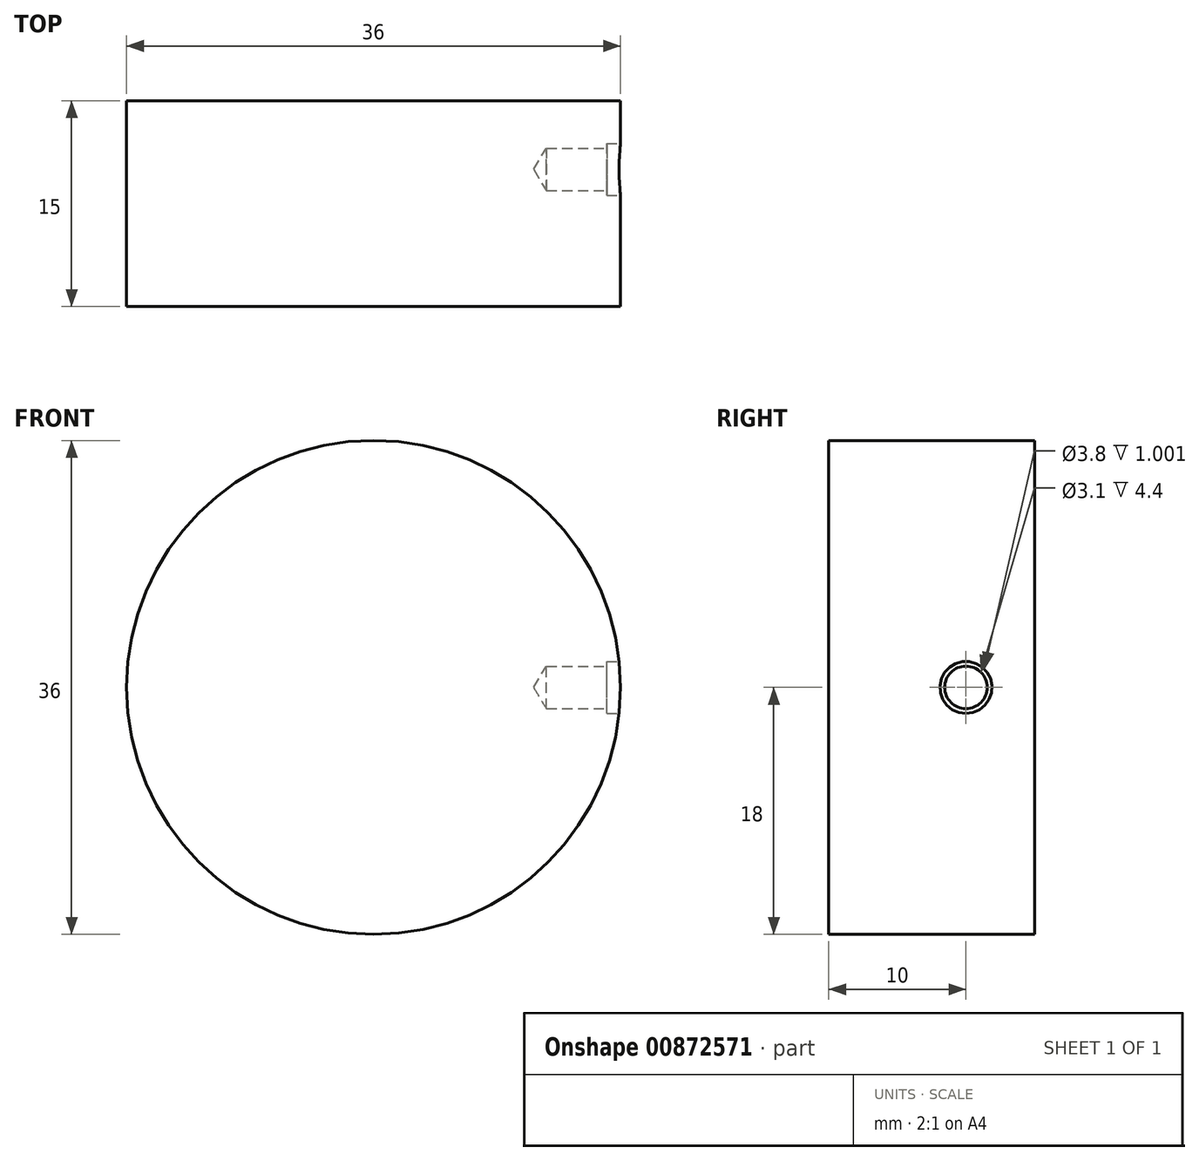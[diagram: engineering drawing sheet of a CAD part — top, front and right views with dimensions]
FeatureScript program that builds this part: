
annotation { "Feature Type Name" : "Feature", "Feature Type Description" : "" }
export const myFeature = defineFeature(function(context is Context, id is Id, definition is map)
    precondition{}
    {
        {
            var Q0;
            Q0=qCreatedBy(makeId("Front.planeOp"),FACE);
            var sketch = newSketch(context, id + "F0", { "sketchPlane" : qUnion([Q0])});
            skCircle(sketch, "E0", {"center": v(0, 0) * mm, "radius": 18 * mm});
            skSolve(sketch);
        }
        {
            var Q0;
            Q0=makeQuery(id+"F0.imprint","IMPRINT",FACE,{"disambiguationData":[TD([[makeQuery(id+"F0.imprint","IMPRINT",EDGE,{"derivedFrom":sQuery(id+"F0.wireOp",EDGE,"E0")}),1.0]])]});
            extrude(context, id + "F1", {"entities" : qUnion([Q0]), "depth" : 15 * mm, "offsetDistance" : 25 * mm});
        }
        {
            var Q0;
            Q0=qCreatedBy(makeId("Right.planeOp"),FACE);
            cPlane(context, id + "F2", {"entities" : qUnion([Q0]), "cplaneType" : CPlaneType.OFFSET, "offset" : 18 * mm, "width" : 150 * mm, "height" : 150 * mm});
        }
        {
            var Q0;
            Q0=qCreatedBy(id+"F2.planeOp",FACE);
            var sketch = newSketch(context, id + "F3", { "sketchPlane" : qUnion([Q0])});
            skCircle(sketch, "E1", {"center": v(-5, 0) * mm, "radius": 1.55 * mm});
            skSolve(sketch);
        }
        {
            var Q0;
            Q0=sQuery(id+"F3.wireOp",VERTEX,"E1.center");
            var Q1;
            Q1=makeQuery(id+"F1.opExtrude","SWEPT_BODY",BODY,{"disambiguationData":[OSD([sQuery(id+"F0.wireOp",EDGE,"E0")])]});
            hole(context, id + "F4", {"style" : HoleStyle.C_BORE, "endStyle" : HoleEndStyle.BLIND, "holeDiameter" : 3.1 * mm, "cBoreDiameter" : 3.8 * mm, "cBoreDepth" : (1) * mm, "majorDiameter" : 5 * mm, "holeDepth" : 5.4 * mm, "isTappedThrough" : true, "tappedDepth" : 12 * mm, "tapClearance" : 3, "startFromSketch" : true, "locations" : qUnion([Q0]), "scope" : qUnion([Q1])});
        }
    });
